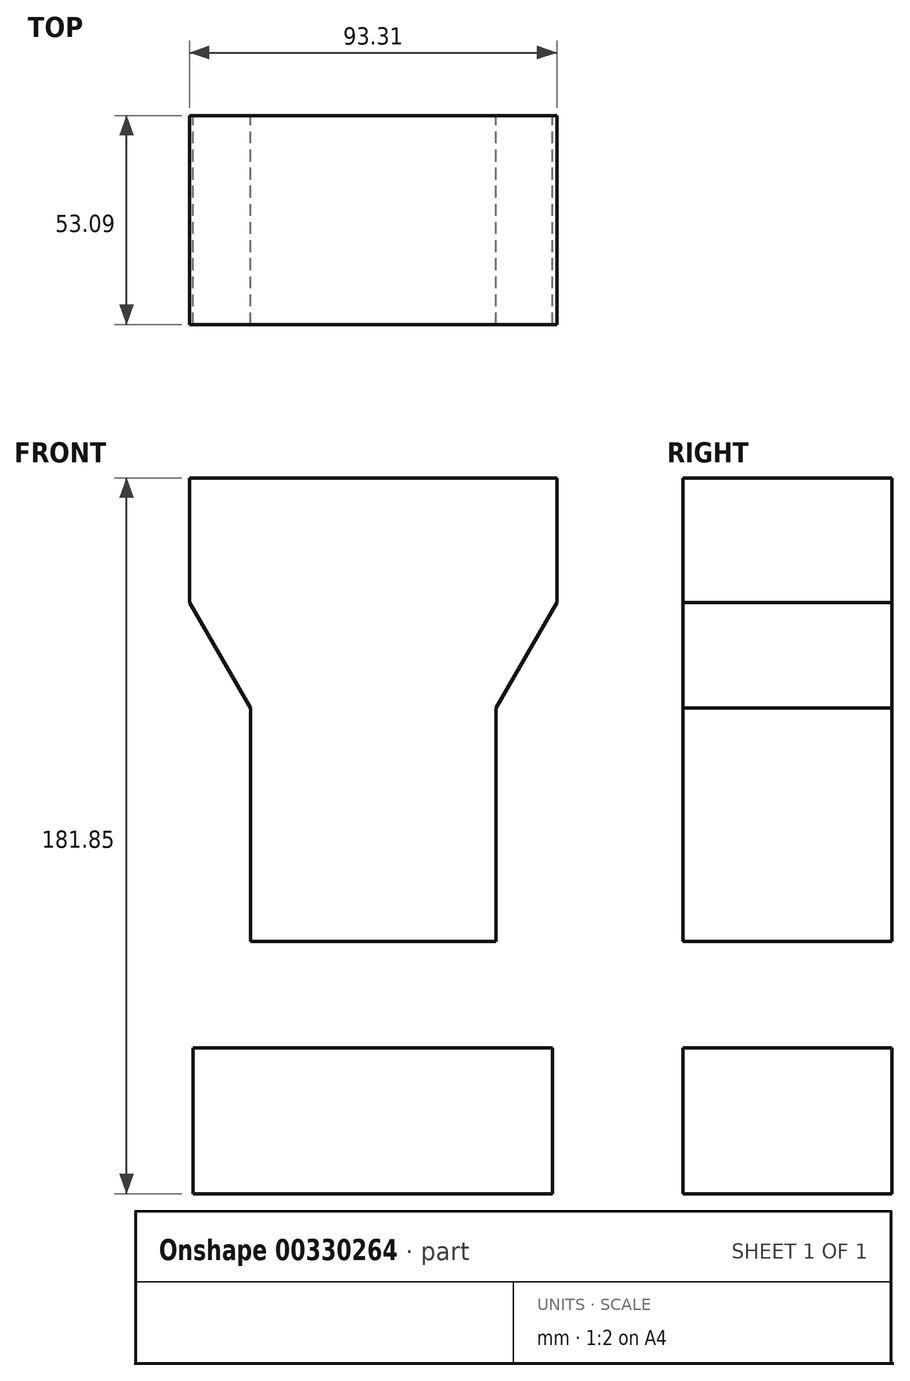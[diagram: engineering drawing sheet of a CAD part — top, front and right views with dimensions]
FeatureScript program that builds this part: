
annotation { "Feature Type Name" : "Feature", "Feature Type Description" : "" }
export const myFeature = defineFeature(function(context is Context, id is Id, definition is map)
    precondition{}
    {
        {
            var Q0;
            Q0=qCreatedBy(makeId("Front.planeOp"),FACE);
            var sketch = newSketch(context, id + "F0", { "sketchPlane" : qUnion([Q0])});
            skLineSegment(sketch, "E0.bottom", {"start": v(-3.95, 19) * mm, "end": v(-97.26, 19) * mm});
            skLineSegment(sketch, "E0.top", {"start": v(-3.95, 50.62) * mm, "end": v(-97.26, 50.62) * mm});
            skLineSegment(sketch, "E0.left", {"start": v(-3.95, 19) * mm, "end": v(-3.95, 50.62) * mm});
            skLineSegment(sketch, "E0.right", {"start": v(-97.26, 19) * mm, "end": v(-97.26, 50.62) * mm});
            skPoint(sketch, "E1.cornerSnap0", {"position": v(-50.6, 19) * mm});
            skLineSegment(sketch, "E2.bottom", {"start": v(-81.84, -7.9) * mm, "end": v(-19.37, -7.9) * mm});
            skLineSegment(sketch, "E2.top", {"start": v(-81.84, -8.68) * mm, "end": v(-19.37, -8.68) * mm});
            skLineSegment(sketch, "E2.left", {"start": v(-81.84, -7.9) * mm, "end": v(-81.84, -8.68) * mm});
            skLineSegment(sketch, "E2.right", {"start": v(-19.37, -7.9) * mm, "end": v(-19.37, -8.68) * mm});
            skPoint(sketch, "E2.middle", {"position": v(-50.6, -8.29) * mm});
            skLineSegment(sketch, "E3", {"start": v(-97.26, 19) * mm, "end": v(-81.84, -7.9) * mm});
            skLineSegment(sketch, "E4", {"start": v(-3.95, 19) * mm, "end": v(-19.37, -7.9) * mm});
            skLineSegment(sketch, "E5", {"start": v(-81.84, -8.68) * mm, "end": v(-81.84, -67.2) * mm});
            skLineSegment(sketch, "E6", {"start": v(-19.37, -7.9) * mm, "end": v(-19.37, -67.2) * mm});
            skLineSegment(sketch, "E7", {"start": v(-81.84, -67.2) * mm, "end": v(-19.37, -67.2) * mm});
            skLineSegment(sketch, "E8", {"start": v(-81.84, -67.2) * mm, "end": v(-96.33, -94.15) * mm});
            skLineSegment(sketch, "E9", {"start": v(-19.37, -67.2) * mm, "end": v(-5.03, -91.3) * mm});
            skLineSegment(sketch, "E10", {"start": v(-96.33, -94.15) * mm, "end": v(-5.03, -94.15) * mm});
            skLineSegment(sketch, "E11", {"start": v(-5.03, -94.15) * mm, "end": v(-5.03, -131.23) * mm});
            skLineSegment(sketch, "E12", {"start": v(-5.03, -131.23) * mm, "end": v(-96.33, -131.23) * mm});
            skLineSegment(sketch, "E13", {"start": v(-96.33, -131.23) * mm, "end": v(-96.33, -94.15) * mm});
            skSolve(sketch);
        }
        {
            var Q0;
            Q0 = qSketchRegion(id + "F0", true);
            extrude(context, id + "F1", {"entities" : qUnion([Q0]), "depth" : 53.1 * mm});
        }
    });
